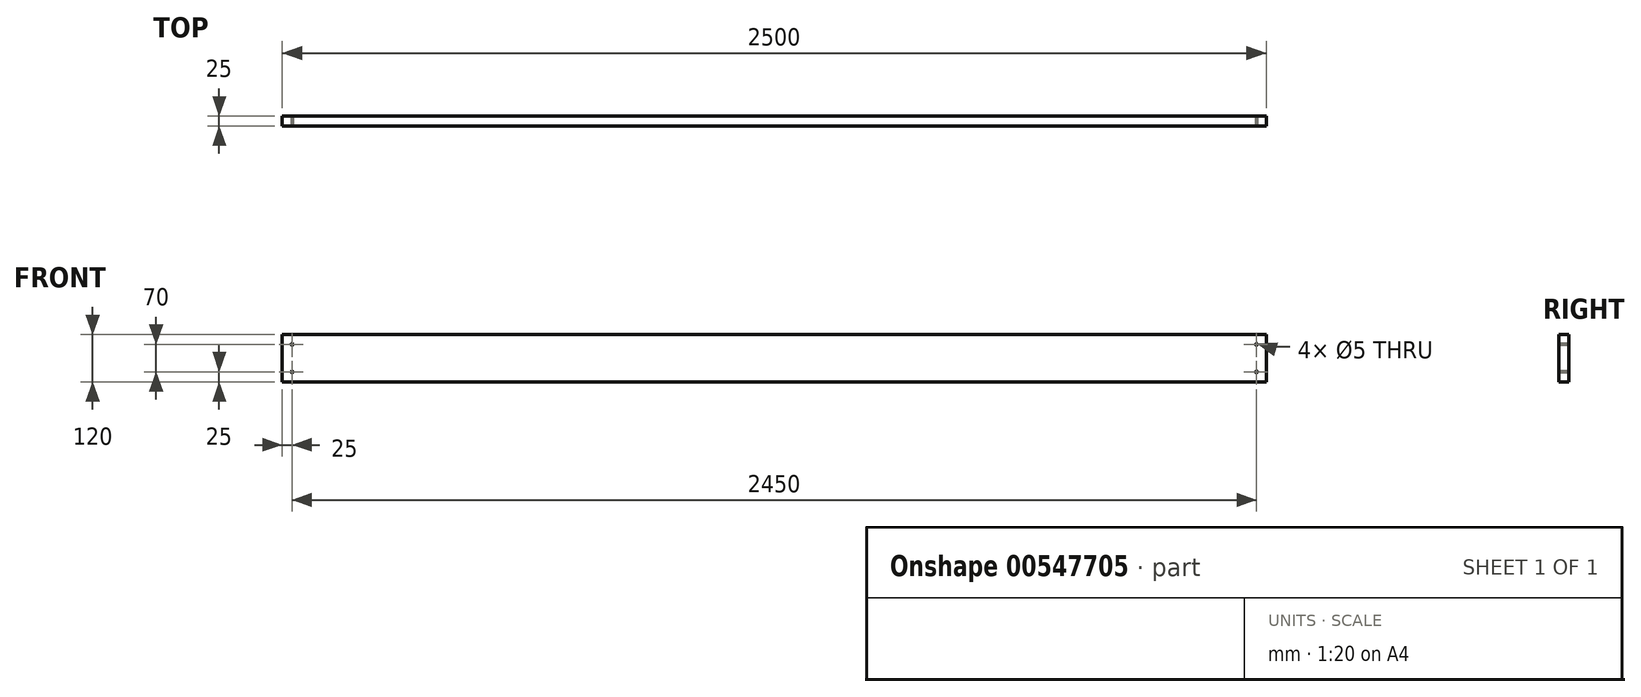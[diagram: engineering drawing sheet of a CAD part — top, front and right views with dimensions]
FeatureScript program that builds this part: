
annotation { "Feature Type Name" : "Feature", "Feature Type Description" : "" }
export const myFeature = defineFeature(function(context is Context, id is Id, definition is map)
    precondition{}
    {
        {
            var Q0;
            Q0=qCreatedBy(makeId("Front.planeOp"),FACE);
            var sketch = newSketch(context, id + "F0", { "sketchPlane" : qUnion([Q0])});
            skLineSegment(sketch, "E0.bottom", {"start": v(1250, 60) * mm, "end": v(-1250, 60) * mm});
            skLineSegment(sketch, "E0.top", {"start": v(1250, -60) * mm, "end": v(-1250, -60) * mm});
            skLineSegment(sketch, "E0.left", {"start": v(1250, 60) * mm, "end": v(1250, -60) * mm});
            skLineSegment(sketch, "E0.right", {"start": v(-1250, 60) * mm, "end": v(-1250, -60) * mm});
            skPoint(sketch, "E0.middle", {"position": v(0, 0) * mm});
            skSolve(sketch);
        }
        {
            var Q0;
            Q0=makeQuery(id+"F0.imprint","IMPRINT",FACE,{"disambiguationData":[TD([[makeQuery(id+"F0.imprint","IMPRINT",EDGE,{"derivedFrom":sQuery(id+"F0.wireOp",EDGE,"E0.bottom")}),1.0]])]});
            extrude(context, id + "F1", {"entities" : qUnion([Q0]), "depth" : 25 * mm, "offsetDistance" : 25 * mm});
        }
        {
            var Q0;
            Q0=makeQuery(id+"F1.opExtrude","CAP_FACE",FACE,{"disambiguationData":[OSD([sQuery(id+"F0.wireOp",EDGE,"E0.bottom"),sQuery(id+"F0.wireOp",EDGE,"E0.top"),sQuery(id+"F0.wireOp",EDGE,"E0.left"),sQuery(id+"F0.wireOp",EDGE,"E0.right")])],"isStart":false});
            var sketch = newSketch(context, id + "F2", { "sketchPlane" : qUnion([Q0])});
            skCircle(sketch, "E1", {"center": v(1225, 35) * mm, "radius": 2.5 * mm});
            skCircle(sketch, "E2", {"center": v(1225, -35) * mm, "radius": 2.5 * mm});
            skLineSegment(sketch, "E3", {"start": v(0, -60) * mm, "end": v(0, 18.14) * mm, "construction": true});
            skPoint(sketch, "E3.endSnap0", {"position": v(0, -60) * mm});
            skCircle(sketch, "E4.MirrorC", {"center": v(-1225, 35) * mm, "radius": 2.5 * mm});
            skCircle(sketch, "E5.MirrorC", {"center": v(-1225, -35) * mm, "radius": 2.5 * mm});
            skSolve(sketch);
        }
        {
            var Q0;
            Q0=sQuery(id+"F2.wireOp",VERTEX,"E5.MirrorC.center");
            var Q1;
            Q1=sQuery(id+"F2.wireOp",VERTEX,"E4.MirrorC.center");
            var Q2;
            Q2=sQuery(id+"F2.wireOp",VERTEX,"E2.center");
            var Q3;
            Q3=sQuery(id+"F2.wireOp",VERTEX,"E1.center");
            var Q4;
            Q4=makeQuery(id+"F1.opExtrude","SWEPT_BODY",BODY,{"disambiguationData":[OSD([sQuery(id+"F0.wireOp",EDGE,"E0.bottom"),sQuery(id+"F0.wireOp",EDGE,"E0.top"),sQuery(id+"F0.wireOp",EDGE,"E0.left"),sQuery(id+"F0.wireOp",EDGE,"E0.right")])]});
            hole(context, id + "F3", {"style" : HoleStyle.SIMPLE, "endStyle" : HoleEndStyle.THROUGH, "holeDiameter" : 5 * mm, "isTappedThrough" : true, "tappedDepth" : 12 * mm, "tapClearance" : 3, "locations" : qUnion([Q0, Q1, Q2, Q3]), "scope" : qUnion([Q4])});
        }
    });
